# Revit family: Haworth_Compose_Panel_DoorPost
name_source: partatom
category: Furniture Systems
revit_build: Autodesk Revit 2018 (Build: 20170223_1515(x64)
units: mm (PartAtom-declared; Revit-internal decimal feet)

## family parameters
Always vertical = Yes
Cut with Voids When Loaded = No
OmniClass Number = 23.40.70.14.64.21
OmniClass Title = Systems Furniture
Part Type = Normal
Room Calculation Point = No
Round Connector Dimension = Use Diameter
Shared = Yes
Work Plane-Based = No

## types (4) — shared parameters
Actual Width = 3"
Assembly Code = E2020500
Custom Size = No
Description = Haworth - Compose Panel - Accessories Door - Post
Manufacturer = Haworth
Max. Height = 90"
Max. Width = 3"
Min. Height = 66"
Min. Width = 3"
Min/Max Height = 66, 74, 82, 90 in.
Model = VZZP
Post Depth = 3"
Post Finish = Haworth _ Paint _ Putty
Revision Number = 5
Size = Verify Final Dim. w/ Haworth
Sustainability Info = http://media.haworth.com
Top Trim Thin Profile = Yes
Top Trim Width = 1/8"
Trim Finish = Haworth _ Paint _ Putty
URL = http://www.haworth.com
URL - Product = http://www.haworth.com
Warranty = http://www.haworth.com

## per-type parameters (varying)
| type | Actual Height | Height |
| 66h | 65 7/8" | 66" |
| 82h | 81 7/8" | 82" |
| 74h | 73 7/8" | 74" |
| 90h | 89 7/8" | 90" |

## geometry (parser evidence)
native form markers: Sweep x3
no freeform markers — native parametric forms only
